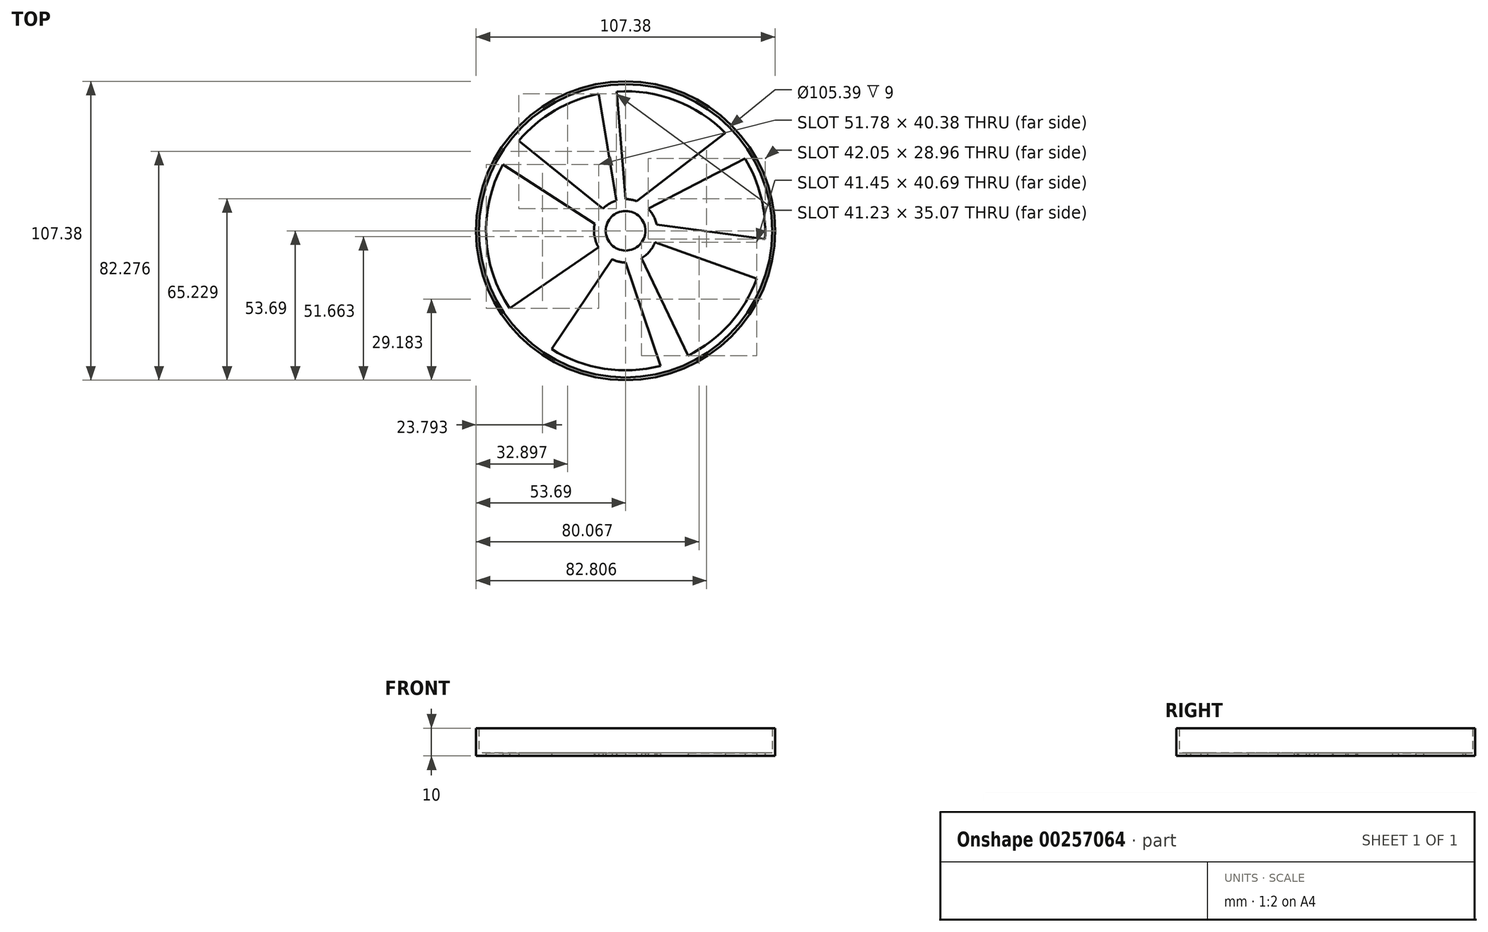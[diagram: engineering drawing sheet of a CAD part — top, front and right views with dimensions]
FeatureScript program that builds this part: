
annotation { "Feature Type Name" : "Feature", "Feature Type Description" : "" }
export const myFeature = defineFeature(function(context is Context, id is Id, definition is map)
    precondition{}
    {
        {
            var Q0;
            Q0=qCreatedBy(makeId("Top.planeOp"),FACE);
            var sketch = newSketch(context, id + "F0", { "sketchPlane" : qUnion([Q0])});
            skLineSegment(sketch, "E0", {"start": v(-4.42, 6.66) * mm, "end": v(0, 20.99) * mm});
            skLineSegment(sketch, "E1", {"start": v(0, 20.99) * mm, "end": v(5.06, 6.66) * mm});
            skLineSegment(sketch, "E2", {"start": v(5.06, 6.66) * mm, "end": v(20.3, 6.66) * mm});
            skLineSegment(sketch, "E3", {"start": v(20.3, 6.66) * mm, "end": v(8.19, -2.21) * mm});
            skLineSegment(sketch, "E4", {"start": v(8.19, -2.21) * mm, "end": v(12.73, -17.14) * mm});
            skLineSegment(sketch, "E5", {"start": v(12.73, -17.14) * mm, "end": v(0, -8.17) * mm});
            skLineSegment(sketch, "E6", {"start": v(0, -8.17) * mm, "end": v(-12.09, -17.14) * mm});
            skLineSegment(sketch, "E7", {"start": v(-12.09, -17.14) * mm, "end": v(-7.75, -2.21) * mm});
            skLineSegment(sketch, "E8", {"start": v(-7.75, -2.21) * mm, "end": v(-19.65, 6.46) * mm});
            skLineSegment(sketch, "E9", {"start": v(-19.65, 6.46) * mm, "end": v(-4.42, 6.66) * mm});
            skSolve(sketch);
        }
        {
            var Q0;
            Q0=makeQuery(id+"F0.imprint","IMPRINT",FACE,{"disambiguationData":[TD([[makeQuery(id+"F0.imprint","IMPRINT",EDGE,{"derivedFrom":sQuery(id+"F0.wireOp",EDGE,"E0")}),-1.0]])]});
            var sketch = newSketch(context, id + "F1", { "sketchPlane" : qUnion([Q0])});
            skCircle(sketch, "E10", {"center": v(0, 0) * mm, "radius": 20.97 * mm});
            skSolve(sketch);
        }
        {
            var Q0;
            Q0=qCreatedBy(makeId("Top.planeOp"),FACE);
            var sketch = newSketch(context, id + "F2", { "sketchPlane" : qUnion([Q0])});
            skCircle(sketch, "E11", {"center": v(0, 0) * mm, "radius": 32.11 * mm});
            skSolve(sketch);
        }
        {
            var Q0;
            Q0=qCreatedBy(makeId("Top.planeOp"),FACE);
            var sketch = newSketch(context, id + "F3", { "sketchPlane" : qUnion([Q0])});
            skCircle(sketch, "E12", {"center": v(0, 0) * mm, "radius": 42.36 * mm});
            skSolve(sketch);
        }
        {
            var Q0;
            Q0=qCreatedBy(makeId("Top.planeOp"),FACE);
            var sketch = newSketch(context, id + "F4", { "sketchPlane" : qUnion([Q0])});
            skCircle(sketch, "E13", {"center": v(0, 0) * mm, "radius": 53.7 * mm});
            skSolve(sketch);
        }
        {
            var Q0;
            Q0=makeQuery(id+"F4.imprint","IMPRINT",FACE,{"disambiguationData":[TD([[makeQuery(id+"F4.imprint","IMPRINT",EDGE,{"derivedFrom":sQuery(id+"F4.wireOp",EDGE,"E13")}),1.0]])]});
            extrude(context, id + "F5", {"entities" : qUnion([Q0]), "depth" : 10 * mm});
        }
        {
            var Q0;
            Q0=makeQuery(id+"F5.opExtrude","CAP_FACE",FACE,{"disambiguationData":[OSD([sQuery(id+"F4.wireOp",EDGE,"E13")])],"isStart":false});
            shell(context, id + "F6", {"entities" : qUnion([Q0]), "thickness" : 1 * mm});
        }
        {
            var Q0;
            Q0=sQuery(id+"F3.wireOp",EDGE,"E12");
            extrude(context, id + "F7", {"bodyType" : ToolBodyType.SURFACE, "surfaceEntities" : qUnion([Q0]), "depth" : 5 * mm});
        }
        {
            var Q0;
            Q0=sQuery(id+"F2.wireOp",EDGE,"E11");
            extrude(context, id + "F8", {"bodyType" : ToolBodyType.SURFACE, "surfaceEntities" : qUnion([Q0]), "depth" : 5 * mm});
        }
        {
            var Q0;
            Q0=sQuery(id+"F1.wireOp",EDGE,"E10");
            extrude(context, id + "F9", {"bodyType" : ToolBodyType.SURFACE, "surfaceEntities" : qUnion([Q0]), "depth" : 5 * mm});
        }
        {
            var Q0;
            Q0=sQuery(id+"F0.wireOp",EDGE,"E8");
            var Q1;
            Q1=sQuery(id+"F0.wireOp",EDGE,"E9");
            var Q2;
            Q2=sQuery(id+"F0.wireOp",EDGE,"E0");
            var Q3;
            Q3=sQuery(id+"F0.wireOp",EDGE,"E1");
            var Q4;
            Q4=sQuery(id+"F0.wireOp",EDGE,"E2");
            var Q5;
            Q5=sQuery(id+"F0.wireOp",EDGE,"E3");
            var Q6;
            Q6=sQuery(id+"F0.wireOp",EDGE,"E4");
            var Q7;
            Q7=sQuery(id+"F0.wireOp",EDGE,"E5");
            var Q8;
            Q8=sQuery(id+"F0.wireOp",EDGE,"E6");
            var Q9;
            Q9=sQuery(id+"F0.wireOp",EDGE,"E7");
            extrude(context, id + "F10", {"bodyType" : ToolBodyType.SURFACE, "surfaceEntities" : qUnion([Q0, Q1, Q2, Q3, Q4, Q5, Q6, Q7, Q8, Q9]), "depth" : 5 * mm});
        }
        {
            var Q0;
            Q0=qCreatedBy(makeId("Top.planeOp"),FACE);
            var sketch = newSketch(context, id + "F11", { "sketchPlane" : qUnion([Q0])});
            skCircle(sketch, "E14", {"center": v(0, 0) * mm, "radius": 7.13 * mm});
            skSolve(sketch);
        }
        {
            var Q0;
            Q0 = qSketchRegion(id + "F11", true);
            extrude(context, id + "F12", {"entities" : qUnion([Q0]), "operationType" : NewBodyOperationType.REMOVE, "oppositeDirection" : true, "depth" : 62.1 * mm});
        }
        {
            var Q0;
            Q0=qCreatedBy(makeId("Top.planeOp"),FACE);
            var sketch = newSketch(context, id + "F13", { "sketchPlane" : qUnion([Q0])});
            skCircle(sketch, "E15", {"center": v(0, 0) * mm, "radius": 7.12 * mm});
            skSolve(sketch);
        }
        {
            var Q0;
            Q0 = qSketchRegion(id + "F13", true);
            extrude(context, id + "F14", {"entities" : qUnion([Q0]), "operationType" : NewBodyOperationType.REMOVE, "depth" : 79.5 * mm});
        }
        {
            var Q0;
            Q0=makeQuery(id+"F5.opExtrude","CAP_FACE",FACE,{"disambiguationData":[OSD([sQuery(id+"F4.wireOp",EDGE,"E13")])],"isStart":true});
            var sketch = newSketch(context, id + "F15", { "sketchPlane" : qUnion([Q0])});
            skCircle(sketch, "E16", {"center": v(0, 0) * mm, "radius": 55 * mm});
            skCircle(sketch, "E17", {"center": v(0, 0) * mm, "radius": 50.15 * mm});
            skCircle(sketch, "E18", {"center": v(0, 0) * mm, "radius": 11.36 * mm});
            skLineSegment(sketch, "E19", {"start": v(8.1, -7.97) * mm, "end": v(42.87, -26.02) * mm});
            skLineSegment(sketch, "E20", {"start": v(3.94, -10.66) * mm, "end": v(35.83, -35.08) * mm});
            skLineSegment(sketch, "E21", {"start": v(-8.1, -7.97) * mm, "end": v(-38.33, -32.33) * mm});
            skLineSegment(sketch, "E22", {"start": v(-11.08, -2.53) * mm, "end": v(-44.1, -23.86) * mm});
            skLineSegment(sketch, "E23", {"start": v(-9.7, 5.9) * mm, "end": v(-41.66, 27.92) * mm});
            skLineSegment(sketch, "E24", {"start": v(-4.86, 10.27) * mm, "end": v(-26.57, 42.53) * mm});
            skLineSegment(sketch, "E25", {"start": v(0, 11.36) * mm, "end": v(12.56, 48.55) * mm});
            skLineSegment(sketch, "E26", {"start": v(5.65, 9.86) * mm, "end": v(22.43, 44.85) * mm});
            skLineSegment(sketch, "E27", {"start": v(10.57, 4.16) * mm, "end": v(47.1, 17.2) * mm});
            skLineSegment(sketch, "E28", {"start": v(11.13, -2.29) * mm, "end": v(50.06, 2.94) * mm});
            skLineSegment(sketch, "E29", {"start": v(-3.26, -10.88) * mm, "end": v(-9.7, -49.2) * mm});
            skLineSegment(sketch, "E30", {"start": v(0, -11.36) * mm, "end": v(-3.18, -50.04) * mm});
            skSolve(sketch);
        }
        {
            var Q0;
            {var subQ0=sQuery(id+"F15.wireOp",EDGE,"E24");Q0=makeQuery(id+"F15.imprint","IMPRINT",FACE,{"disambiguationData":[TD([[makeQuery(id+"F15.imprint","IMPRINT",EDGE,{"derivedFrom":subQ0}),-1.0]])]});}
            var Q1;
            {var subQ0=sQuery(id+"F15.wireOp",EDGE,"E22");Q1=makeQuery(id+"F15.imprint","IMPRINT",FACE,{"disambiguationData":[TD([[makeQuery(id+"F15.imprint","IMPRINT",EDGE,{"derivedFrom":subQ0}),-1.0]])]});}
            var Q2;
            {var subQ0=sQuery(id+"F15.wireOp",EDGE,"E21");Q2=makeQuery(id+"F15.imprint","IMPRINT",FACE,{"disambiguationData":[TD([[makeQuery(id+"F15.imprint","IMPRINT",EDGE,{"derivedFrom":subQ0}),1.0]])]});}
            var Q3;
            {var subQ0=sQuery(id+"F15.wireOp",EDGE,"E20");Q3=makeQuery(id+"F15.imprint","IMPRINT",FACE,{"disambiguationData":[TD([[makeQuery(id+"F15.imprint","IMPRINT",EDGE,{"derivedFrom":subQ0}),-1.0]])]});}
            var Q4;
            {var subQ0=sQuery(id+"F15.wireOp",EDGE,"E19");Q4=makeQuery(id+"F15.imprint","IMPRINT",FACE,{"disambiguationData":[TD([[makeQuery(id+"F15.imprint","IMPRINT",EDGE,{"derivedFrom":subQ0}),1.0]])]});}
            var Q5;
            {var subQ0=sQuery(id+"F15.wireOp",EDGE,"E26");Q5=makeQuery(id+"F15.imprint","IMPRINT",FACE,{"disambiguationData":[TD([[makeQuery(id+"F15.imprint","IMPRINT",EDGE,{"derivedFrom":subQ0}),-1.0]])]});}
            extrude(context, id + "F16", {"entities" : qUnion([Q0, Q1, Q2, Q3, Q4, Q5]), "operationType" : NewBodyOperationType.REMOVE, "oppositeDirection" : true, "depth" : 25 * mm});
        }
    });
